# Revit family: FU_Chair_Sandler_Varya XL 0040
name_source: partatom
category: Furniture
units: mm (PartAtom-declared; Revit-internal decimal feet)

## family parameters
Always vertical = Yes
Cut with Voids When Loaded = No
OmniClass Number = 23.40.20.00
OmniClass Title = General Furniture and Specialties
Render Appearance Source = Family Geometry
Room Calculation Point = No
Shared = No
Work Plane-Based = No

## types (1)
- Varya XL 0040
    Default Elevation = 0 mm  [stored 0 ft]
    Depth = 525 mm
    Description = Stackable armchair with polypropylene shell and upholstered seat. Aluminum armpads and round steel tube 4 leg frame. Greenguard Gold Certified.
    Height = 830 mm  [stored 2.7231 ft]
    Manufacturer = Sandler
    Model = Varya XL 0040
    URL = https://www.sandlerseating.com
    Width = 690 mm  [stored 2.26378 ft]

note: [stored X ft] marks values corroborated as IEEE doubles in the binary element streams (Revit-internal decimal feet)

## geometry (parser evidence)
native form markers: Sweep x5
no freeform markers — native parametric forms only
